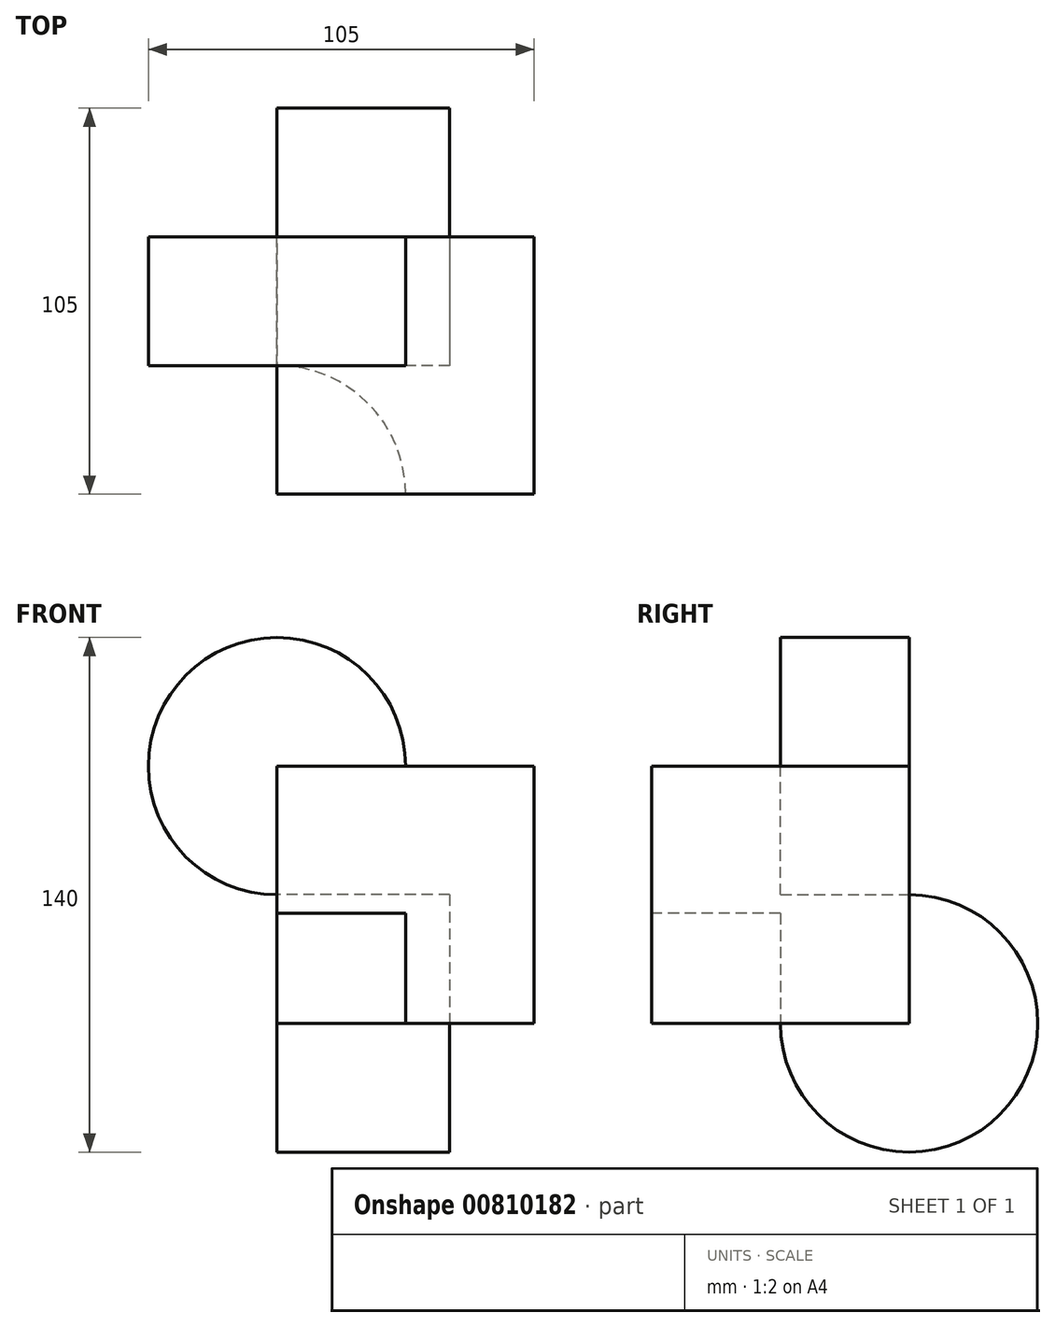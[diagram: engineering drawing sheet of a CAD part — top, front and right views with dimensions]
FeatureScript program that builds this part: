
annotation { "Feature Type Name" : "Feature", "Feature Type Description" : "" }
export const myFeature = defineFeature(function(context is Context, id is Id, definition is map)
    precondition{}
    {
        {
            var Q0;
            Q0=qCreatedBy(makeId("Top.planeOp"),FACE);
            var sketch = newSketch(context, id + "F0", { "sketchPlane" : qUnion([Q0])});
            skLineSegment(sketch, "E0.bottom", {"start": v(35, 35) * mm, "end": v(-35, 35) * mm});
            skLineSegment(sketch, "E0.top", {"start": v(35, -35) * mm, "end": v(-35, -35) * mm});
            skLineSegment(sketch, "E0.left", {"start": v(35, 35) * mm, "end": v(35, -35) * mm});
            skLineSegment(sketch, "E0.right", {"start": v(-35, 35) * mm, "end": v(-35, -35) * mm});
            skPoint(sketch, "E0.middle", {"position": v(0, 0) * mm});
            skSolve(sketch);
        }
        {
            var Q0;
            Q0=makeQuery(id+"F0.imprint","IMPRINT",FACE,{"disambiguationData":[TD([[makeQuery(id+"F0.imprint","IMPRINT",EDGE,{"derivedFrom":sQuery(id+"F0.wireOp",EDGE,"E0.bottom")}),1.0]])]});
            extrude(context, id + "F1", {"entities" : qUnion([Q0]), "depth" : 70 * mm, "offsetDistance" : 25.4 * mm});
        }
        {
            var Q0;
            Q0=makeQuery(id+"F1.opExtrude","CAP_FACE",FACE,{"disambiguationData":[OSD([sQuery(id+"F0.wireOp",EDGE,"E0.bottom"),sQuery(id+"F0.wireOp",EDGE,"E0.top"),sQuery(id+"F0.wireOp",EDGE,"E0.left"),sQuery(id+"F0.wireOp",EDGE,"E0.right")])],"isStart":true});
            var sketch = newSketch(context, id + "F2", { "sketchPlane" : qUnion([Q0])});
            skCircle(sketch, "E1", {"center": v(-35, 35) * mm, "radius": 35 * mm});
            skSolve(sketch);
        }
        {
            var Q0;
            {var subQ0=sQuery(id+"F2.wireOp",EDGE,"E1");var subQ1=makeQuery(id+"F1.opExtrude","CAP_EDGE",EDGE,{"disambiguationData":[OSD([sQuery(id+"F0.wireOp",EDGE,"E0.top")])],"isStart":true});var subQ2=makeQuery(id+"F2.imprint","INTERSECT",VERTEX,{"derivedFrom":[subQ1,subQ0]});Q0=makeQuery(id+"F2.imprint","IMPRINT",FACE,{"disambiguationData":[TD([[makeQuery(id+"F2.imprint","IMPRINT",EDGE,{"disambiguationData":[TD([[subQ2,1.0]])],"derivedFrom":subQ0}),1.0]])]});}
            extrude(context, id + "F3", {"entities" : qUnion([Q0]), "operationType" : NewBodyOperationType.REMOVE, "oppositeDirection" : true, "depth" : 29.97 * mm, "offsetDistance" : 25.4 * mm});
        }
        {
            var Q0;
            Q0=makeQuery(id+"F1.opExtrude","SWEPT_FACE",FACE,{"disambiguationData":[OSD([sQuery(id+"F0.wireOp",EDGE,"E0.bottom")])]});
            var sketch = newSketch(context, id + "F4", { "sketchPlane" : qUnion([Q0])});
            skCircle(sketch, "E2", {"center": v(35, 70) * mm, "radius": 35 * mm});
            skSolve(sketch);
        }
        {
            var Q0;
            Q0 = qSketchRegion(id + "F4", true);
            extrude(context, id + "F5", {"entities" : qUnion([Q0]), "oppositeDirection" : true, "depth" : 35 * mm, "offsetDistance" : 25.4 * mm});
        }
        {
            var Q0;
            Q0=makeQuery(id+"F1.opExtrude","SWEPT_FACE",FACE,{"disambiguationData":[OSD([sQuery(id+"F0.wireOp",EDGE,"E0.right")])]});
            var sketch = newSketch(context, id + "F6", { "sketchPlane" : qUnion([Q0])});
            skCircle(sketch, "E3", {"center": v(-35, 0) * mm, "radius": 35 * mm});
            skSolve(sketch);
        }
        {
            var Q0;
            Q0 = qSketchRegion(id + "F6", true);
            extrude(context, id + "F7", {"entities" : qUnion([Q0]), "operationType" : NewBodyOperationType.ADD, "oppositeDirection" : true, "depth" : 47 * mm, "offsetDistance" : 25.4 * mm});
        }
    });
